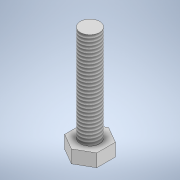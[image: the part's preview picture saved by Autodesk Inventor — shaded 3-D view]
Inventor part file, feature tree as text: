
AUTODESK INVENTOR PART (.ipt)
format: ipt  version: 2020.2 (Build 242310000, 310)  size: 124,928 bytes
history: native  units: mm
features: extrude x2, sketch x2, thread x1
ambient origin geometry x8: Origin, YZ Plane, XZ Plane, XY Plane, X Axis, Y Axis, Z Axis, Center Point
bodies: Solido1 (feature_tree)
feature tree (5):
  extrude  "Estrusione1"  Depth=10.0mm
  extrude  "Estrusione2"  Depth=4.0mm TaperAngle=0.0deg
  thread  "Filettatura1"
  sketch  "Schizzo1"
  sketch  "Schizzo2"
